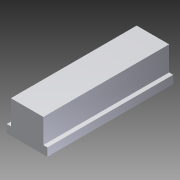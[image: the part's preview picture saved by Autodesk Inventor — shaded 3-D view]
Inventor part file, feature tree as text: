
AUTODESK INVENTOR PART (.ipt)
format: ipt  version: 2012 (Build 160160000, 160)  size: 78,336 bytes
history: native  units: in
note: dims shown in document units (in); Inventor stores cm internally (conversion verified against a paired STEP export)
features: extrude x1, sketch x1
ambient origin geometry x8: Origin, YZ Plane, XZ Plane, XY Plane, X Axis, Y Axis, Z Axis, Center Point
bodies: Solid1 (feature_tree)
feature tree (2):
  extrude  "Extrusion1"  Depth=1.0in
  sketch  "Sketch1"  dims[d0=1.25in d1=1.0in d2=0.25in d3=0.125in d4=3.875in d5=0.0in]
